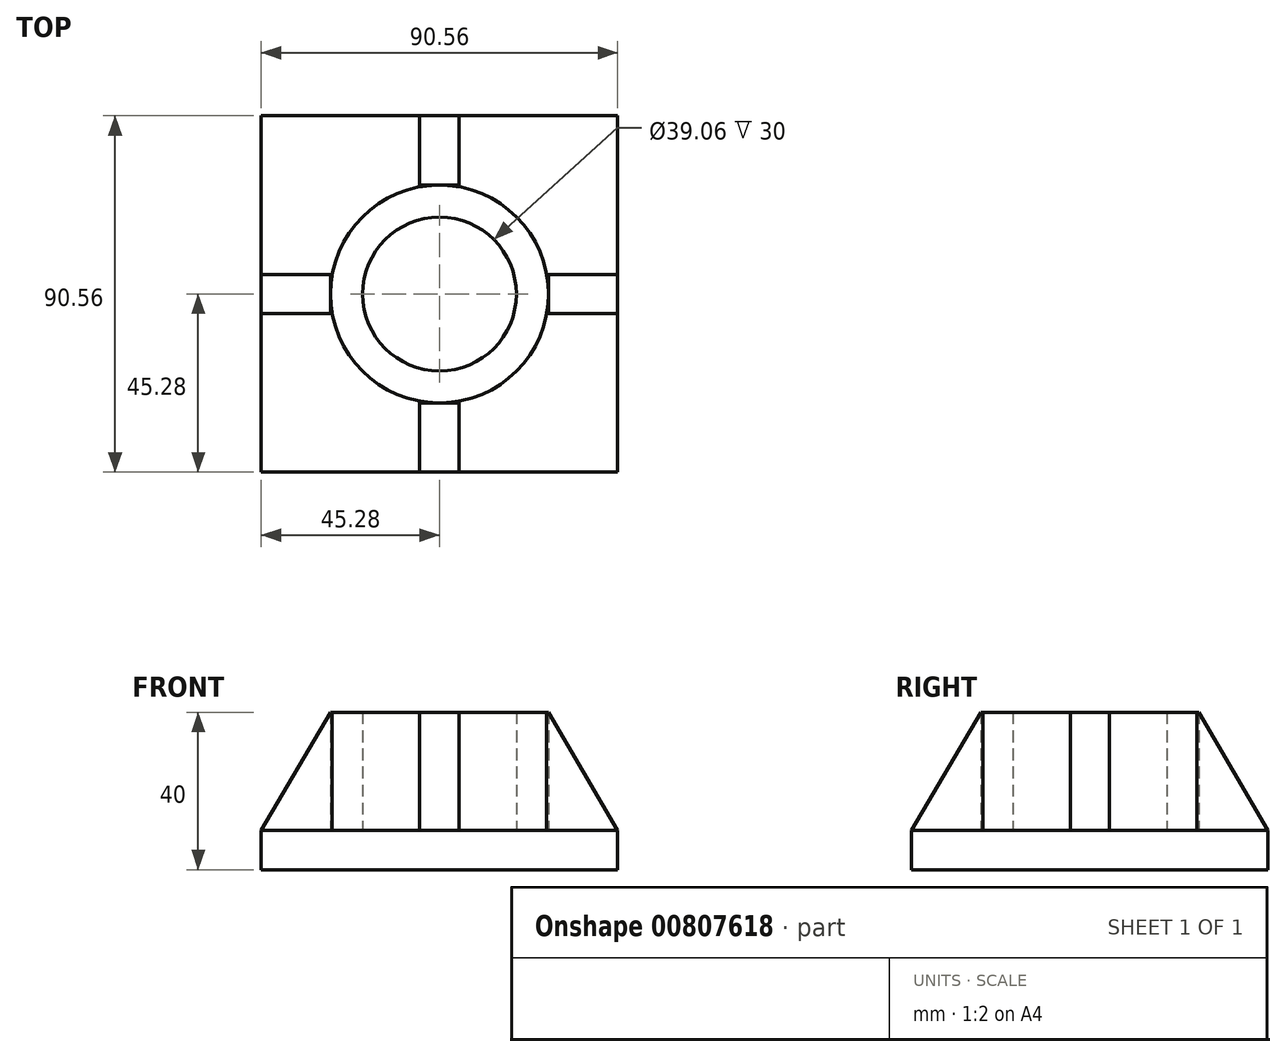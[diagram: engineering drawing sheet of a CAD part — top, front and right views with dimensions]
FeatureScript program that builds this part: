
annotation { "Feature Type Name" : "Feature", "Feature Type Description" : "" }
export const myFeature = defineFeature(function(context is Context, id is Id, definition is map)
    precondition{}
    {
        {
            var Q0;
            Q0=qCreatedBy(makeId("Top.planeOp"),FACE);
            var sketch = newSketch(context, id + "F0", { "sketchPlane" : qUnion([Q0])});
            skLineSegment(sketch, "E0.bottom", {"start": v(45.28, 45.28) * mm, "end": v(-45.28, 45.28) * mm});
            skLineSegment(sketch, "E0.top", {"start": v(45.28, -45.28) * mm, "end": v(-45.28, -45.28) * mm});
            skLineSegment(sketch, "E0.left", {"start": v(45.28, 45.28) * mm, "end": v(45.28, -45.28) * mm});
            skLineSegment(sketch, "E0.right", {"start": v(-45.28, 45.28) * mm, "end": v(-45.28, -45.28) * mm});
            skPoint(sketch, "E0.middle", {"position": v(0, 0) * mm});
            skCircle(sketch, "E1", {"center": v(0, 0) * mm, "radius": 19.53 * mm});
            skCircle(sketch, "E2", {"center": v(0, 0) * mm, "radius": 27.69 * mm});
            skSolve(sketch);
        }
        {
            var Q0;
            Q0=makeQuery(id+"F0.imprint","IMPRINT",FACE,{"disambiguationData":[TD([[makeQuery(id+"F0.imprint","IMPRINT",EDGE,{"derivedFrom":sQuery(id+"F0.wireOp",EDGE,"E0.bottom")}),1.0]])]});
            var Q1;
            Q1=makeQuery(id+"F0.imprint","IMPRINT",FACE,{"disambiguationData":[TD([[makeQuery(id+"F0.imprint","IMPRINT",EDGE,{"derivedFrom":sQuery(id+"F0.wireOp",EDGE,"E1")}),-1.0]])]});
            var Q2;
            Q2=makeQuery(id+"F0.imprint","IMPRINT",FACE,{"disambiguationData":[TD([[makeQuery(id+"F0.imprint","IMPRINT",EDGE,{"derivedFrom":sQuery(id+"F0.wireOp",EDGE,"E1")}),1.0]])]});
            extrude(context, id + "F1", {"entities" : qUnion([Q0, Q1, Q2]), "depth" : 10 * mm, "offsetDistance" : 25 * mm});
        }
        {
            var Q0;
            Q0=makeQuery(id+"F1.opExtrude","CAP_FACE",FACE,{"disambiguationData":[OSD([sQuery(id+"F0.wireOp",EDGE,"E0.bottom"),sQuery(id+"F0.wireOp",EDGE,"E0.top"),sQuery(id+"F0.wireOp",EDGE,"E0.left"),sQuery(id+"F0.wireOp",EDGE,"E0.right")])],"isStart":false});
            var sketch = newSketch(context, id + "F2", { "sketchPlane" : qUnion([Q0])});
            skCircle(sketch, "E3.0", {"center": v(0, 0) * mm, "radius": 27.69 * mm});
            skCircle(sketch, "E4.0", {"center": v(0, 0) * mm, "radius": 19.53 * mm});
            skSolve(sketch);
        }
        {
            var Q0;
            Q0 = qSketchRegion(id + "F2", true);
            extrude(context, id + "F3", {"entities" : qUnion([Q0]), "depth" : 30 * mm, "offsetDistance" : 25 * mm});
        }
        {
            var Q0;
            Q0=qCreatedBy(makeId("Front.planeOp"),FACE);
            var sketch = newSketch(context, id + "F4", { "sketchPlane" : qUnion([Q0])});
            skPoint(sketch, "E5.0", {"position": v(-45.28, 10) * mm});
            skLineSegment(sketch, "E6.0", {"start": v(-27.69, 40) * mm, "end": v(27.69, 40) * mm});
            skLineSegment(sketch, "E7", {"start": v(-27.69, 10) * mm, "end": v(-27.69, 40) * mm});
            skLineSegment(sketch, "E8.0", {"start": v(45.28, 10) * mm, "end": v(-45.28, 10) * mm});
            skLineSegment(sketch, "E9", {"start": v(-45.28, 10) * mm, "end": v(-27.69, 40) * mm});
            skLineSegment(sketch, "E10", {"start": v(-23.51, 40) * mm, "end": v(-23.51, 10) * mm});
            skLineSegment(sketch, "E11", {"start": v(0, 0) * mm, "end": v(0, 55.97) * mm, "construction": true});
            skSolve(sketch);
        }
        {
            var Q0;
            Q0 = qSketchRegion(id + "F4", true);
            extrude(context, id + "F5", {"entities" : qUnion([Q0]), "depth" : 10 * mm, "offsetDistance" : 25 * mm, "symmetric" : true});
        }
        {
            var Q0;
            Q0=makeQuery(id+"F3.opExtrude","SWEPT_BODY",BODY,{"disambiguationData":[OSD([sQuery(id+"F2.wireOp",EDGE,"E3.0"),sQuery(id+"F2.wireOp",EDGE,"E4.0")])]});
            var Q1;
            Q1=makeQuery(id+"F5.opExtrude","SWEPT_BODY",BODY,{"disambiguationData":[OSD([sQuery(id+"F4.wireOp",EDGE,"E6.0"),sQuery(id+"F4.wireOp",EDGE,"E8.0"),sQuery(id+"F4.wireOp",EDGE,"E9"),sQuery(id+"F4.wireOp",EDGE,"E10")])]});
            booleanBodies(context, id + "F6", {"operationType" : BooleanOperationType.SUBTRACTION, "tools" : qUnion([Q0]), "targets" : qUnion([Q1]), "keepTools" : true});
        }
        {
            var Q0;
            Q0=makeQuery(id+"F5.opExtrude","SWEPT_BODY",BODY,{"disambiguationData":[OSD([sQuery(id+"F4.wireOp",EDGE,"E6.0"),sQuery(id+"F4.wireOp",EDGE,"E8.0"),sQuery(id+"F4.wireOp",EDGE,"E9"),sQuery(id+"F4.wireOp",EDGE,"E10")])]});
            var Q1;
            Q1=sQuery(id+"F4.wireOp",EDGE,"E11");
            circularPattern(context, id + "F7", {"entities" : qUnion([Q0]), "axis" : qUnion([Q1]), "angle" : 360 * degree, "instanceCount" : 4, "equalSpace" : true, "computeTransformsWithoutBuiltin" : true});
        }
    });
